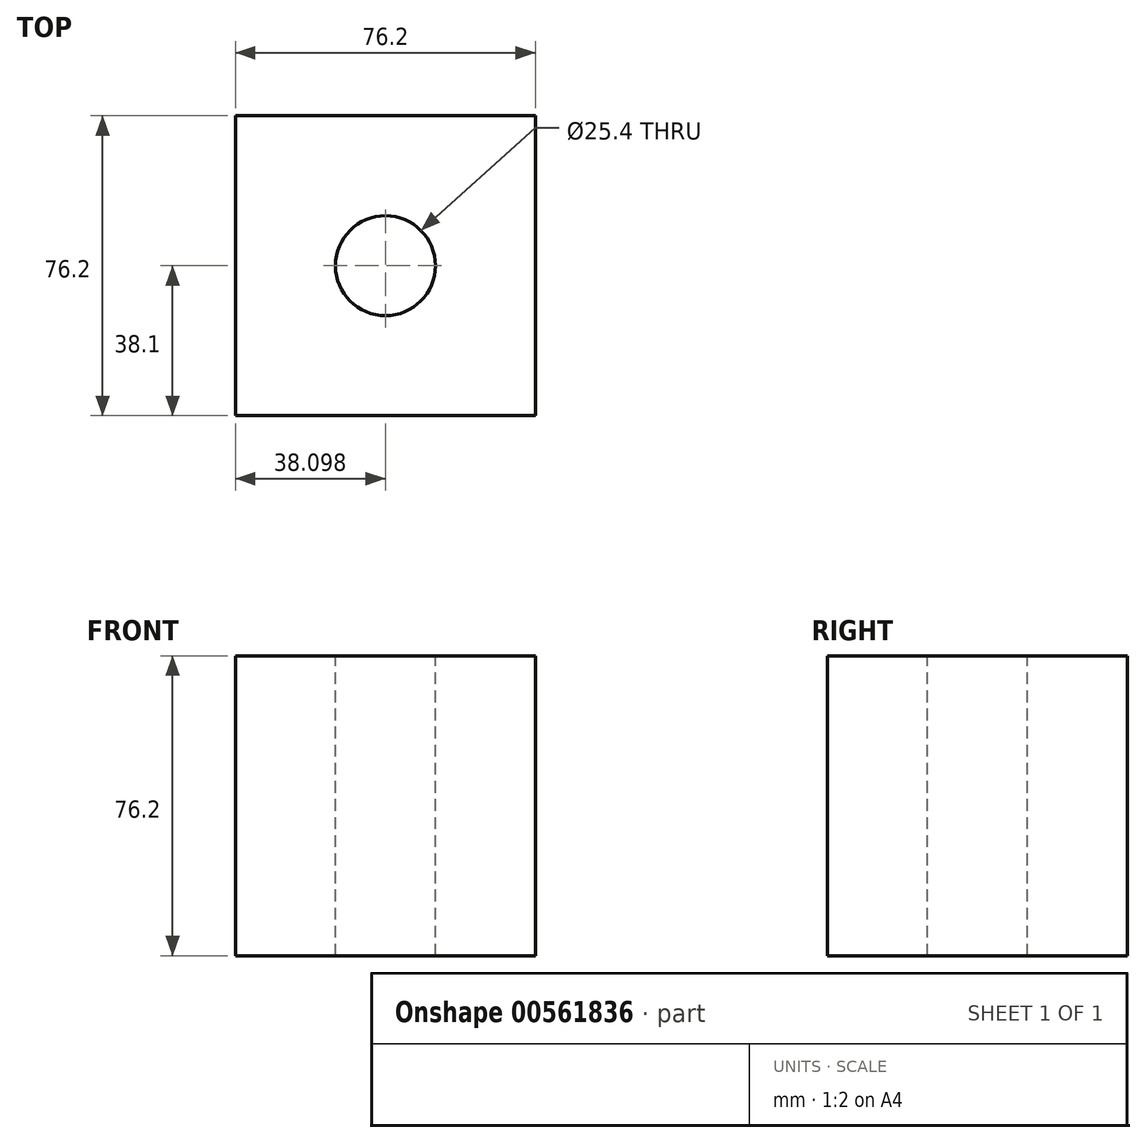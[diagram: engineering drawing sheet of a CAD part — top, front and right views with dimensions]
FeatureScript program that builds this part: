
annotation { "Feature Type Name" : "Feature", "Feature Type Description" : "" }
export const myFeature = defineFeature(function(context is Context, id is Id, definition is map)
    precondition{}
    {
        {
            var Q0;
            Q0=qCreatedBy(makeId("Front.planeOp"),FACE);
            var sketch = newSketch(context, id + "F0", { "sketchPlane" : qUnion([Q0])});
            skLineSegment(sketch, "E0.bottom", {"start": v(-99.42, -41.18) * mm, "end": v(-23.22, -41.18) * mm});
            skLineSegment(sketch, "E0.top", {"start": v(-99.42, 35.02) * mm, "end": v(-23.22, 35.02) * mm});
            skLineSegment(sketch, "E0.left", {"start": v(-99.42, -41.18) * mm, "end": v(-99.42, 35.02) * mm});
            skLineSegment(sketch, "E0.right", {"start": v(-23.22, -41.18) * mm, "end": v(-23.22, 35.02) * mm});
            skSolve(sketch);
        }
        {
            var Q0;
            Q0=makeQuery(id+"F0.imprint","IMPRINT",FACE,{"disambiguationData":[TD([[makeQuery(id+"F0.imprint","IMPRINT",EDGE,{"derivedFrom":sQuery(id+"F0.wireOp",EDGE,"E0.bottom")}),1.0]])]});
            extrude(context, id + "F1", {"entities" : qUnion([Q0]), "depth" : 76.2 * mm, "offsetDistance" : 25.4 * mm});
        }
        {
            var Q0;
            Q0=makeQuery(id+"F1.opExtrude","SWEPT_FACE",FACE,{"disambiguationData":[OSD([sQuery(id+"F0.wireOp",EDGE,"E0.top")])]});
            var sketch = newSketch(context, id + "F2", { "sketchPlane" : qUnion([Q0])});
            skPoint(sketch, "E1", {"position": v(-61.32, -38.1) * mm});
            skSolve(sketch);
        }
        {
            var Q0;
            Q0=sQuery(id+"F2.wireOp",VERTEX,"E1");
            var Q1;
            Q1=makeQuery(id+"F1.opExtrude","SWEPT_BODY",BODY,{"disambiguationData":[OSD([sQuery(id+"F0.wireOp",EDGE,"E0.bottom"),sQuery(id+"F0.wireOp",EDGE,"E0.top"),sQuery(id+"F0.wireOp",EDGE,"E0.left"),sQuery(id+"F0.wireOp",EDGE,"E0.right")])]});
            hole(context, id + "F3", {"style" : HoleStyle.SIMPLE, "endStyle" : HoleEndStyle.THROUGH, "holeDiameter" : 25.4 * mm, "isTappedThrough" : true, "tappedDepth" : 12.7 * mm, "tapClearance" : 3, "locations" : qUnion([Q0]), "scope" : qUnion([Q1])});
        }
    });
